# Revit family: HERZ Strömax Балансировочный клапан с измерительными клапанами, шпиндель прямой 4218 GMF
name_source: partatom
category: Rohrzubehör
revit_build: Autodesk Revit 2018 (Build: 20190510_1515(x64)
units: mm (PartAtom-declared; Revit-internal decimal feet)

## family parameters
Arbeitsebenenbasiert = Nein
Beim Laden mit Abzugskörper schneiden = Nein
Bemaßung runder Anschluss = Durchmesser verwenden
Gemeinsam genutzt = Nein
Immer vertikal = Ja
OmniClass-Nummer = 23.65.55.14
OmniClass-Titel = Valves for Liquid Services
Teiletyp = Unterbricht

## types (1)
- HERZ Strömax Балансировочный клапан с измерительными клапанами, шпиндель прямой 4218 GMF
    GT = 10 mm  [stored 0.0328084 ft]
    H07 = 10 mm  [stored 0.0328084 ft]
    Hersteller = HERZ Armaturen Ges.m.b.H.
    O-Ring = EPDM
    SCRNCODE = 05;07;02
    SCRNSEQ = ARM;ARM_TYP="STRV";2
    URL = www.herz-armaturen.ru
    W02 = 60.00°
    Букса (до DN100) = латунь
    Букса (от DN125) = чугун
    Измерение перепада давления = Клапан балансировочный STRÖMAX-GMF укомплектован двумя измерительными клапанами:
при применении соответствующего измерительного прибора можно измерить перепад давления и по диаграмме определить текущий расход в зависимости от ступени настройки.
На экране измерительного прибора высвечивается текущее значение расхода (см. руководство по измерительным приборам).
    Исполнение = STRÖMAX-GMF-Балансировочный клапан с измерительными клапанами DN 25 - 150:
Шпиндель прямой, корпус из чугуна GJL 250 по EN 1561, фланцевое исполнение EN 1092, PN 16, синего цвета.
Буксы клапана до DN 100 из латуни, резьбовое соединение, от DN 125 буксы клапана из чугуна, с неподнимающимся шпинделем.
Уплотнение шпинделя при помощи двойного кольцевого уплотнения.
Предварительная настройка производится посредством ограничения хода с помощью внутреннего шпинделя, цифровые показания ступени преднастройки считываются в окошке маховика.
Два измерительных клапана монтируются сверху, по обе стороны маховика.
    Корпус = чугун GJL 250 по EN 1561
    Макс. рабочая температура (до DN32) = 130 °C
    Макс. рабочая температура (с DN40) = 110 °C
    Макс. рабочее давление = 1600000.0 Pa
    Область применения = Для гидравлической балансировки в системах отопления или охлаждения, регулирования и перекрытия трубопроводов, стояков, теплообменников, регистров отопления и охлаждения.
    Среда = Допускается использование этилен- и пропиленгликоля в концентрации смеси 25-50% объема.
Качество теплоносителя в соответствии с ÖNORM H 5195 и VDI 2035.

note: [stored X ft] marks values corroborated as IEEE doubles in the binary element streams (Revit-internal decimal feet)
